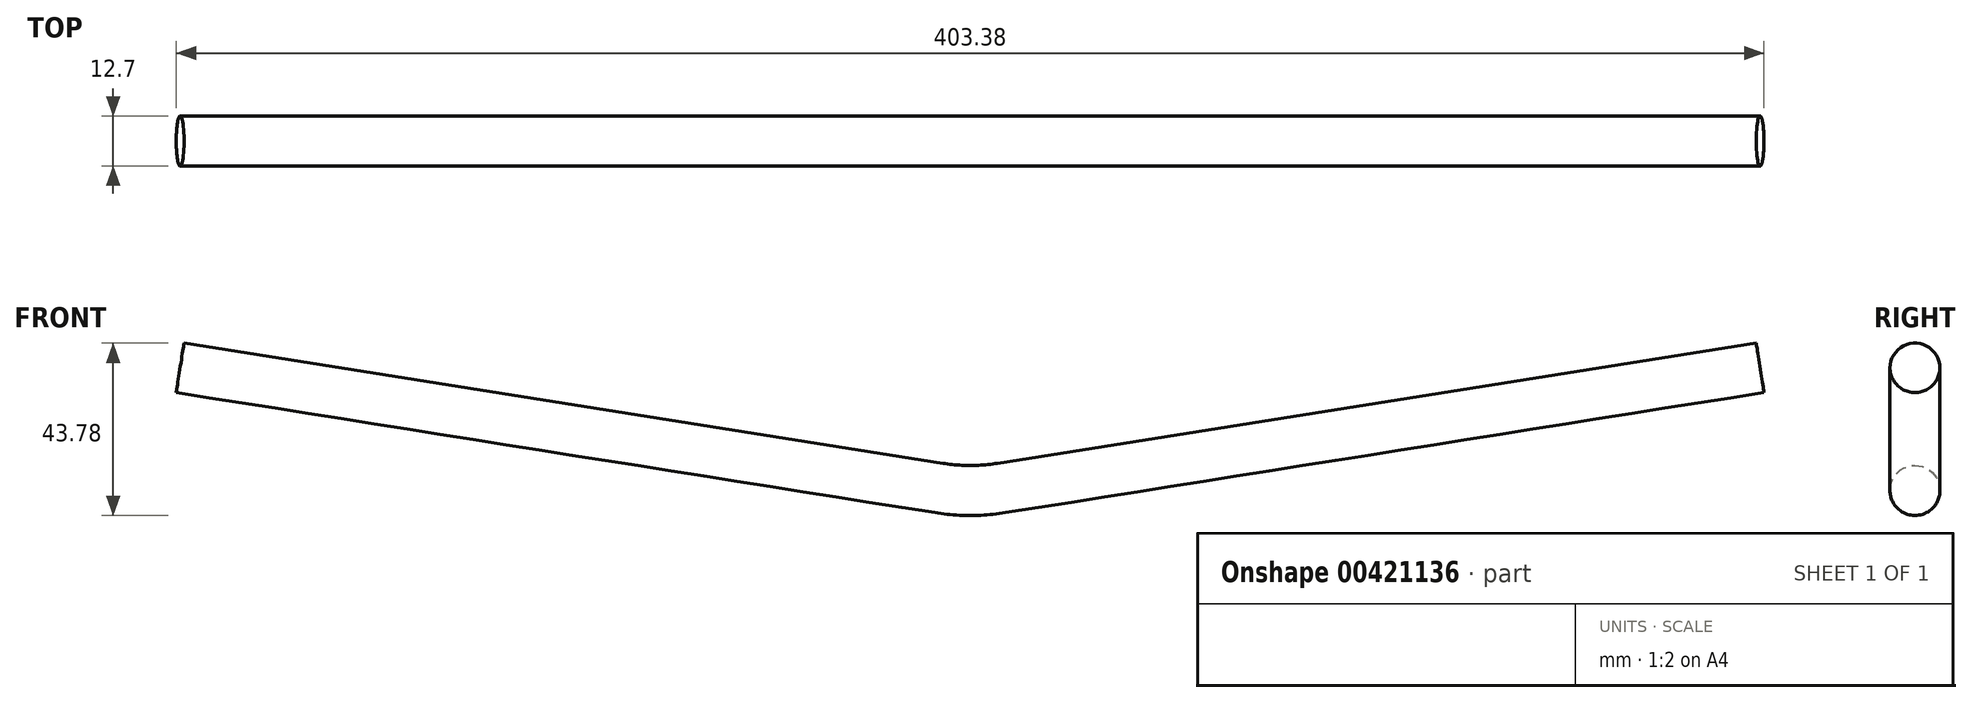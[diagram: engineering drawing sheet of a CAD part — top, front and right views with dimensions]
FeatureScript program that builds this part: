
annotation { "Feature Type Name" : "Feature", "Feature Type Description" : "" }
export const myFeature = defineFeature(function(context is Context, id is Id, definition is map)
    precondition{}
    {
        {
            var Q0;
            Q0=qCreatedBy(makeId("Front.planeOp"),FACE);
            var sketch = newSketch(context, id + "F0", { "sketchPlane" : qUnion([Q0])});
            skLineSegment(sketch, "E0", {"start": v(-200.7, 31.79) * mm, "end": v(-3.97, 0.63) * mm, "construction": true});
            skLineSegment(sketch, "E1", {"start": v(0, 0) * mm, "end": v(-191.82, 0) * mm, "construction": true});
            skLineSegment(sketch, "E2", {"start": v(-185.16, 129.92) * mm, "end": v(-227.22, -135.68) * mm, "construction": true});
            skLineSegment(sketch, "E3", {"start": v(0, 43.45) * mm, "end": v(0, 0) * mm, "construction": true});
            skLineSegment(sketch, "E4.MirrorCS", {"start": v(200.7, 31.79) * mm, "end": v(3.97, 0.63) * mm, "construction": true});
            skPoint(sketch, "E5.visualSharp", {"position": v(0, 0) * mm});
            skArc(sketch, "E5.filletArc", {"start": v(-3.97, 0.63) * mm, "mid": v(0, 0.32) * mm, "end": v(3.97, 0.63) * mm, "construction": true});
            skSolve(sketch);
        }
        {
            var Q0;
            Q0=sQuery(id+"F0.wireOp",VERTEX,"E0.start");
            var Q1;
            Q1=sQuery(id+"F0.wireOp",EDGE,"E0");
            cPlane(context, id + "F1", {"entities" : qUnion([Q0, Q1]), "cplaneType" : CPlaneType.LINE_POINT, "offset" : 25.4 * mm, "width" : 152.4 * mm, "height" : 152.4 * mm});
        }
        {
            var Q0;
            Q0=qCreatedBy(id+"F1.planeOp",FACE);
            var sketch = newSketch(context, id + "F2", { "sketchPlane" : qUnion([Q0])});
            skCircle(sketch, "E6", {"center": v(0, 0) * mm, "radius": 6.35 * mm});
            skSolve(sketch);
        }
        {
            var Q0;
            Q0=qCreatedBy(makeId("Front.planeOp"),FACE);
            var sketch = newSketch(context, id + "F3", { "sketchPlane" : qUnion([Q0])});
            skLineSegment(sketch, "E7", {"start": v(-7.95, 1.26) * mm, "end": v(-200.7, 31.79) * mm});
            skLineSegment(sketch, "E8", {"start": v(7.95, 1.26) * mm, "end": v(200.7, 31.79) * mm});
            skPoint(sketch, "E9.visualSharp", {"position": v(0, 0) * mm});
            skArc(sketch, "E9.filletArc", {"start": v(-7.95, 1.26) * mm, "mid": v(0, 0.63) * mm, "end": v(7.95, 1.26) * mm});
            skSolve(sketch);
        }
        {
            var Q0;
            Q0=makeQuery(id+"F2.imprint","IMPRINT",FACE,{"disambiguationData":[TD([[makeQuery(id+"F2.imprint","IMPRINT",EDGE,{"derivedFrom":sQuery(id+"F2.wireOp",EDGE,"E6")}),1.0]])]});
            var Q1;
            Q1=sQuery(id+"F3.wireOp",EDGE,"E7");
            var Q2;
            Q2=sQuery(id+"F3.wireOp",EDGE,"E9.filletArc");
            var Q3;
            Q3=sQuery(id+"F3.wireOp",EDGE,"E8");
            sweep(context, id + "F4", {"profiles" : qUnion([Q0]), "path" : qUnion([Q1, Q2, Q3])});
        }
    });
